# Revit family: IS_Ceraplus_A3732_BIM_FR
name_source: partatom
category: Plumbing Fixtures
revit_build: Autodesk Revit MEP 2016 (Build: 20161004_0715(x64)
units: mm (PartAtom-declared; Revit-internal decimal feet)

## family parameters
Always vertical = No
Cut with Voids When Loaded = No
OmniClass Number = 23.45.55.14
OmniClass Title = Single Faucets
Part Type = Normal
Room Calculation Point = No
Round Connector Dimension = Use Diameter
Shared = No
Work Plane-Based = No

## types (1)
- A3732XJ - CERAPLUS RUB.ELETTR.INCX ORINATOIO CR
    Accessoires = www.idealspec.fr
    Bim-NomDuProjet = ISI_IdealStandard_Ceraplus_A3732
    Caractéristiques = Capteur Électronique Pour Urinoir
    CodeBarre = 4015413937894
    Conformité = NF
    ConseilsDInstallation = 0
    Cost = 0 $
    Couleur = Chrome
    CoûtDeRemplacement = 0
    DateDeCréation = 43351
    Description = Capteur Électronique Pour Urinoir
    Dimensions = 0 x 0 x 0 mm
    Espace = Interne
    Finition = Chrome
    Forme = Complexe
    Hauteur = 0 mm  [stored 0 ft]
    IfcExportAs = IfcValveType
    IfcExportType = 0
    InformationsProduit = www.idealspec.fr
    Largeur = 0 mm  [stored 0 ft]
    Longueur = 0 mm  [stored 0 ft]
    Marque = Ideal Standard
    Matériel = laiton sanitaire
    Model = A3732XJ
    PoidsNet = 0
    Profondeur = 0 mm  [stored 0 ft]
    Raccordement = Plomberie
    Révision = 1
    URL = www.idealspec.fr
    Uniclass2015Code = Pr_40_20_93_82
    Uniclass2015Title = Wall-hung urinals
    UnitéDeMesure = Millimètres
    UnitéDeTemps = An
    UnitéMonétaire = €
    UrlDuFabricant = www.idealspec.fr

note: [stored X ft] marks values corroborated as IEEE doubles in the binary element streams (Revit-internal decimal feet)

## geometry (parser evidence)
native form markers: Blend x4, Sweep x1
no freeform markers — native parametric forms only
